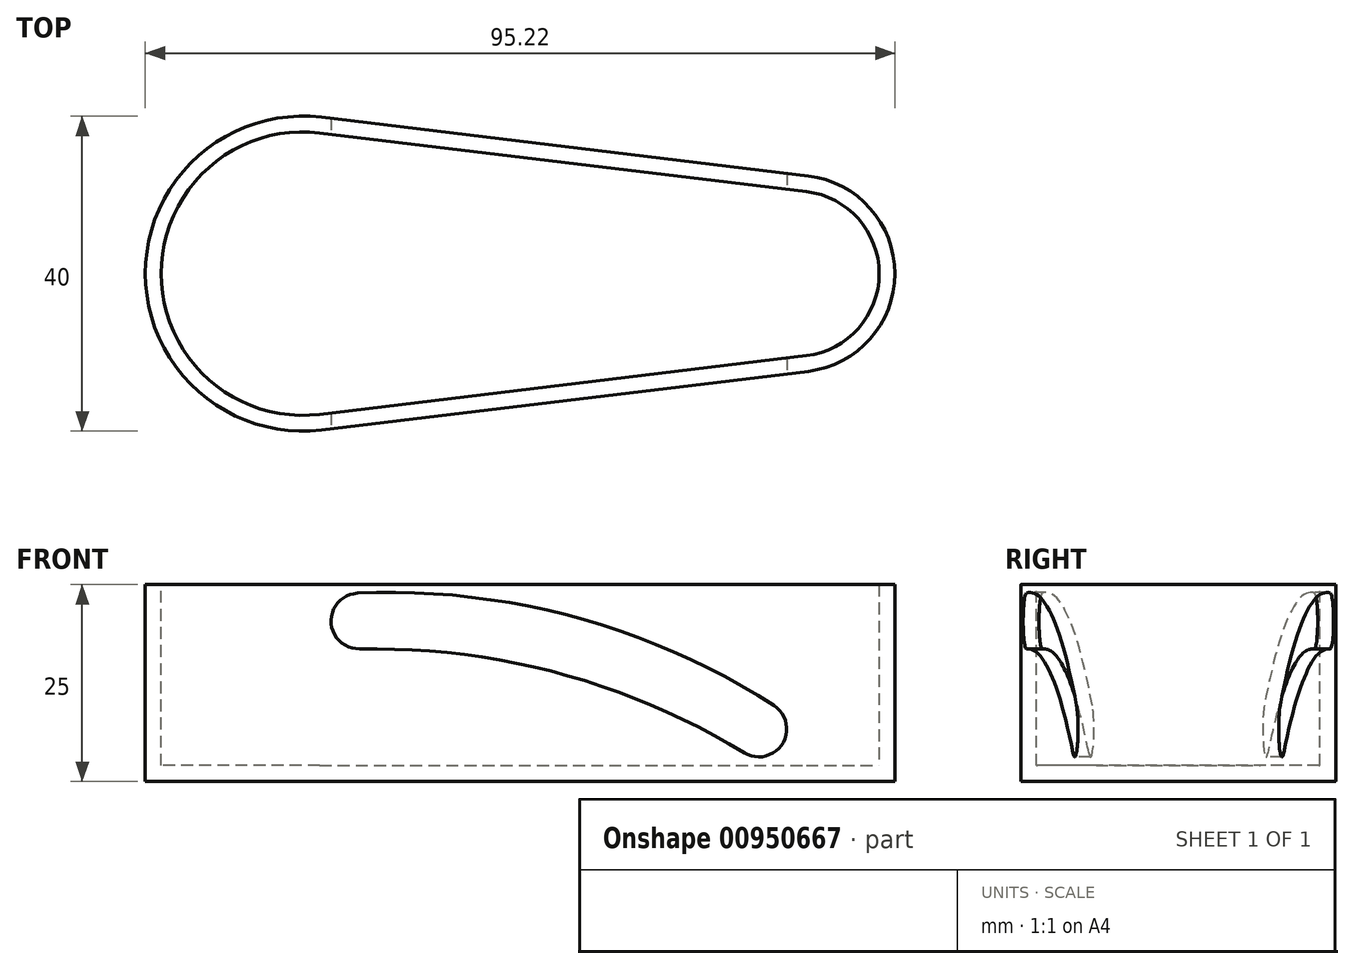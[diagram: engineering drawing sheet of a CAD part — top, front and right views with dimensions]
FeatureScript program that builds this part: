
annotation { "Feature Type Name" : "Feature", "Feature Type Description" : "" }
export const myFeature = defineFeature(function(context is Context, id is Id, definition is map)
    precondition{}
    {
        {
            var Q0;
            Q0=qCreatedBy(makeId("Top.planeOp"),FACE);
            var sketch = newSketch(context, id + "F0", { "sketchPlane" : qUnion([Q0])});
            skArc(sketch, "E0", {"start": v(2.4, 19.86) * mm, "mid": v(-20, 0) * mm, "end": v(2.4, -19.86) * mm});
            skArc(sketch, "E1", {"start": v(64.21, -12.41) * mm, "mid": v(75.22, 0) * mm, "end": v(64.21, 12.41) * mm});
            skLineSegment(sketch, "E2", {"start": v(2.4, 19.86) * mm, "end": v(64.21, 12.41) * mm});
            skLineSegment(sketch, "E3", {"start": v(64.21, -12.41) * mm, "end": v(2.4, -19.86) * mm});
            skSolve(sketch);
        }
        {
            var Q0;
            Q0=makeQuery(id+"F0.imprint","IMPRINT",FACE,{"disambiguationData":[TD([[makeQuery(id+"F0.imprint","IMPRINT",EDGE,{"derivedFrom":sQuery(id+"F0.wireOp",EDGE,"E0")}),1.0]])]});
            extrude(context, id + "F1", {"entities" : qUnion([Q0]), "depth" : 25 * mm, "offsetDistance" : 25 * mm, "hasDraft" : true, "draftAngle" : 0 * radian, "draftPullDirection" : true, "hasSecondDirectionOffset" : true, "secondDirectionOffsetDistance" : 10 * mm, "hasSecondDirectionDraft" : true, "secondDirectionDraftAngle" : 0 * radian});
        }
        {
            var Q0;
            Q0=makeQuery(id+"F1.opExtrude","CAP_FACE",FACE,{"disambiguationData":[OSD([sQuery(id+"F0.wireOp",EDGE,"E0"),sQuery(id+"F0.wireOp",EDGE,"E1"),sQuery(id+"F0.wireOp",EDGE,"E2"),sQuery(id+"F0.wireOp",EDGE,"E3")])],"isStart":false});
            shell(context, id + "F2", {"entities" : qUnion([Q0]), "thickness" : 2 * mm});
        }
        {
            var Q0;
            Q0=qCreatedBy(makeId("Front.planeOp"),FACE);
            var sketch = newSketch(context, id + "F3", { "sketchPlane" : qUnion([Q0])});
            skArc(sketch, "E4", {"start": v(6.95, 23.91) * mm, "mid": v(3.57, 20.24) * mm, "end": v(7.2, 16.82) * mm});
            skArc(sketch, "E5", {"start": v(56.08, 3.62) * mm, "mid": v(60.94, 4.76) * mm, "end": v(59.86, 9.63) * mm});
            skArc(sketch, "E6", {"start": v(59.86, 9.63) * mm, "mid": v(34.52, 20.9) * mm, "end": v(6.95, 23.91) * mm});
            skArc(sketch, "E7", {"start": v(56.08, 3.62) * mm, "mid": v(32.59, 13.73) * mm, "end": v(7.2, 16.82) * mm});
            skSolve(sketch);
        }
        {
            var Q0;
            Q0=makeQuery(id+"F3.imprint","IMPRINT",FACE,{"disambiguationData":[TD([[makeQuery(id+"F3.imprint","IMPRINT",EDGE,{"derivedFrom":sQuery(id+"F3.wireOp",EDGE,"E4")}),1.0]])]});
            extrude(context, id + "F4", {"entities" : qUnion([Q0]), "operationType" : NewBodyOperationType.REMOVE, "endBound" : BoundingType.SYMMETRIC, "oppositeDirection" : true, "depth" : 40.6 * mm, "offsetDistance" : 25 * mm});
        }
    });
